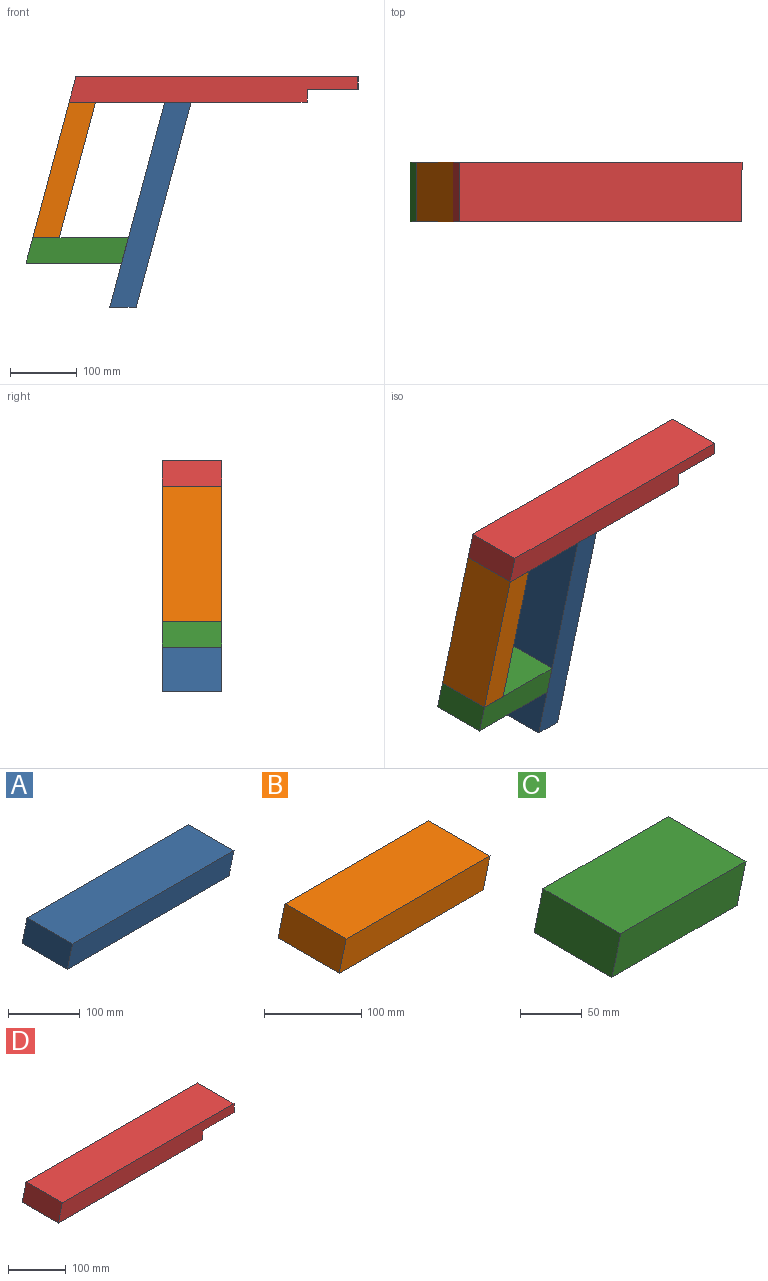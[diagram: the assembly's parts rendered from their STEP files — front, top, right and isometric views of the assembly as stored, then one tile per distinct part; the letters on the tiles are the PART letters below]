
ASSEMBLY  parts=4 mates=3
PART A: 6 faces, bbox 327.7x88.9x38.1 mm
  f0: plane 88.9x38.1mm, normal (-0.97,0,0.26), area 3506.6mm2, adj f1,f3,f4,f5
  f1: plane 317.5x88.9mm, normal (0,0,-1), area 28225.8mm2, adj f0,f2,f4,f5
  f2: plane 88.9x38.1mm, normal (0.97,0,-0.26), area 3506.6mm2, adj f1,f3,f4,f5
  f3: plane 317.5x88.9mm, normal (0,0,1), area 28225.8mm2, adj f0,f2,f4,f5
  f4: plane 327.71x38.1mm, normal (0,-1,0), area 12096.7mm2, adj f0,f1,f2,f3
  f5: plane 327.71x38.1mm, normal (0,1,0), area 12096.7mm2, adj f0,f1,f2,f3
PART B: 6 faces, bbox 219.8x88.9x38.1 mm
  f0: plane 88.9x38.1mm, normal (-0.97,0,0.26), area 3506.6mm2, adj f1,f3,f4,f5
  f1: plane 209.55x88.9mm, normal (0,0,-1), area 18629mm2, adj f0,f2,f4,f5
  f2: plane 88.9x38.1mm, normal (0.97,0,-0.26), area 3506.6mm2, adj f1,f3,f4,f5
  f3: plane 209.55x88.9mm, normal (0,0,1), area 18629mm2, adj f0,f2,f4,f5
  f4: plane 219.76x38.1mm, normal (0,-1,0), area 7983.9mm2, adj f0,f1,f2,f3
  f5: plane 219.76x38.1mm, normal (0,1,0), area 7983.9mm2, adj f0,f1,f2,f3
PART C: 6 faces, bbox 153.1x88.9x38.1 mm
  f0: plane 88.9x38.1mm, normal (-0.97,0,0.26), area 3506.6mm2, adj f1,f3,f4,f5
  f1: plane 142.88x88.9mm, normal (0,0,-1), area 12701.6mm2, adj f0,f2,f4,f5
  f2: plane 88.9x38.1mm, normal (0.97,0,-0.26), area 3506.6mm2, adj f1,f3,f4,f5
  f3: plane 142.88x88.9mm, normal (0,0,1), area 12701.6mm2, adj f0,f2,f4,f5
  f4: plane 153.08x38.1mm, normal (0,-1,0), area 5443.5mm2, adj f0,f1,f2,f3
  f5: plane 153.08x38.1mm, normal (0,1,0), area 5443.5mm2, adj f0,f1,f2,f3
PART D: 8 faces, bbox 431.8x88.9x38.1 mm
  f0: plane 355.6x88.9mm, normal (0,0,-1), area 31612.8mm2, adj f1,f3,f4,f7
  f1: plane 88.9x38.1mm, normal (-0.97,0,0.26), area 3506.6mm2, adj f0,f2,f3,f4
  f2: plane 421.59x88.9mm, normal (0,0,1), area 37479.5mm2, adj f1,f3,f4,f5
  f3: plane 431.8x38.1mm, normal (0,-1,0), area 14805.5mm2, adj f0,f1,f2,f5,f6,f7
  f4: plane 431.8x38.1mm, normal (0,1,0), area 14805.5mm2, adj f0,f1,f2,f5,f6,f7
  f5: plane 88.9x19.05mm, normal (1,0,0), area 1693.5mm2, adj f2,f3,f4,f6
  f6: plane 88.9x76.2mm, normal (0,0,-1), area 6774.2mm2, adj f3,f4,f5,f7
  f7: plane 88.9x19.05mm, normal (1,0,0), area 1693.5mm2, adj f0,f3,f4,f6
PLACE A rot(axis=(-0.79,0,-0.61),180deg) t=(235.52,131.7,-248.02)mm
PLACE B rot(axis=(0.79,0,0.61),180deg) t=(120.59,131.7,-143.75)mm
PLACE C t=(110.38,220.6,-181.85)mm
PLACE D t=(174.82,220.6,58.66)mm
MATE fastened B.f1 <-> D.f1  axis (-0.97,0,0.26) through (174.82,176.15,58.66)mm
MATE fastened D.f0 <-> A.f2  axis (0,0,-1) through (174.82,176.15,58.66)mm
MATE fastened C.f3 <-> B.f0  axis (0,0,1) through (120.59,176.15,-143.75)mm
